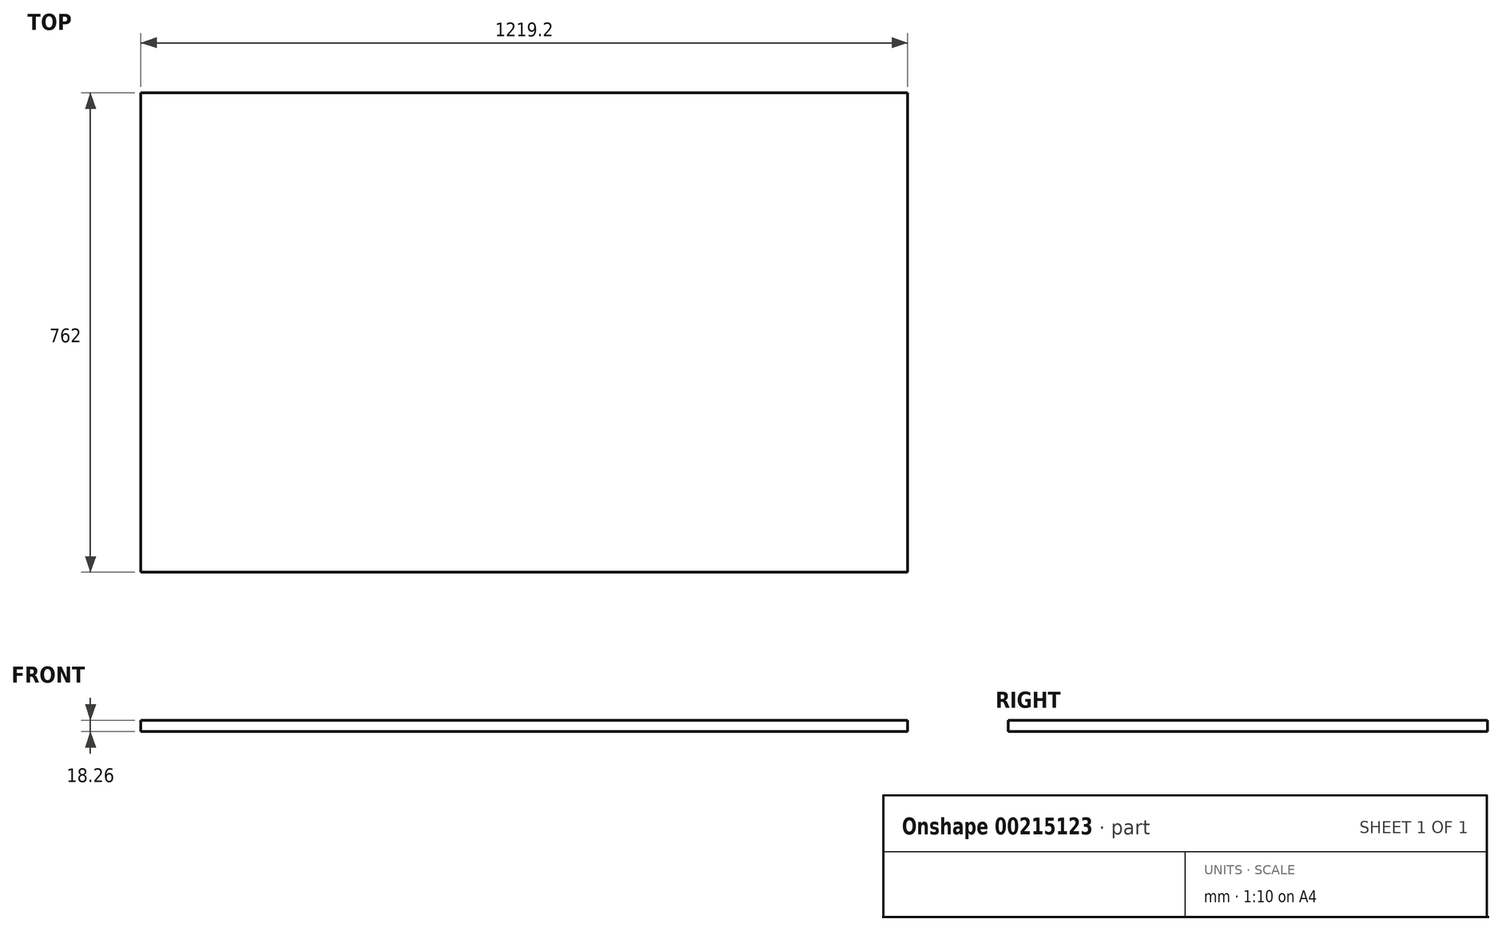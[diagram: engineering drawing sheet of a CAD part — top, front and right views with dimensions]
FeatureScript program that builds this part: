
annotation { "Feature Type Name" : "Feature", "Feature Type Description" : "" }
export const myFeature = defineFeature(function(context is Context, id is Id, definition is map)
    precondition{}
    {
        {
            var Q0;
            Q0=qCreatedBy(makeId("Top.planeOp"),FACE);
            var sketch = newSketch(context, id + "F0", { "sketchPlane" : qUnion([Q0])});
            skLineSegment(sketch, "E0.bottom", {"start": v(0, 0) * mm, "end": v(1219.2, 0) * mm});
            skLineSegment(sketch, "E0.top", {"start": v(0, 762) * mm, "end": v(1219.2, 762) * mm});
            skLineSegment(sketch, "E0.left", {"start": v(0, 0) * mm, "end": v(0, 762) * mm});
            skLineSegment(sketch, "E0.right", {"start": v(1219.2, 0) * mm, "end": v(1219.2, 762) * mm});
            skSolve(sketch);
        }
        {
            var Q0;
            Q0=makeQuery(id+"F0.imprint","IMPRINT",FACE,{"disambiguationData":[TD([[makeQuery(id+"F0.imprint","IMPRINT",EDGE,{"derivedFrom":sQuery(id+"F0.wireOp",EDGE,"E0.bottom")}),1.0]])]});
            extrude(context, id + "F1", {"entities" : qUnion([Q0]), "depth" : 18.26 * mm, "offsetDistance" : 25.4 * mm});
        }
    });
